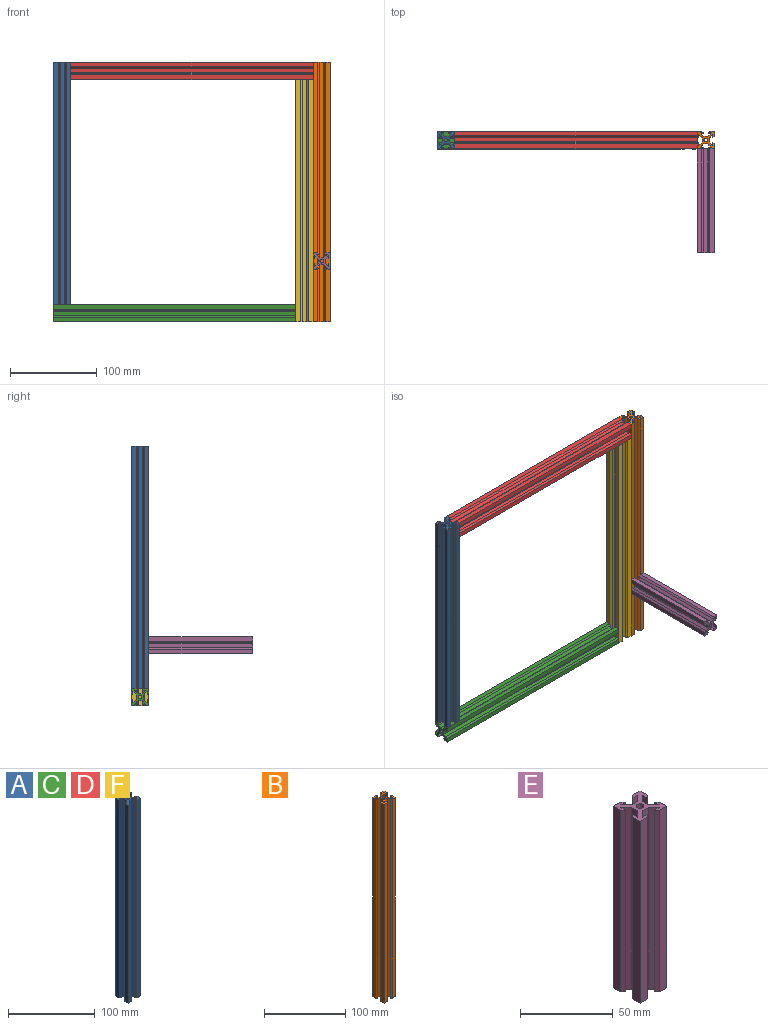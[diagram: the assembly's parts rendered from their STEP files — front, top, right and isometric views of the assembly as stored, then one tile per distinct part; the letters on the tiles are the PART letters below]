
ASSEMBLY  parts=6 mates=5
PART A: 39 faces, bbox 20x20x280 mm
  f0: plane 280x1.8mm, normal (-0.71,0.71,0), area 712.8mm2, adj f1,f35,f37,f38
  f1: plane 280x3.66mm, normal (0,-1,0), area 1023.5mm2, adj f0,f2,f37,f38
  f2: plane 280x4.2mm, normal (-0.71,0.71,0), area 1663.1mm2, adj f1,f3,f37,f38
  f3: plane 280x4.59mm, normal (0,1,0), area 1285.5mm2, adj f2,f4,f37,f38
  f4: plane 280x4.2mm, normal (0.71,0.71,0), area 1663.1mm2, adj f3,f5,f37,f38
  f5: plane 280x3.66mm, normal (0,-1,0), area 1023.5mm2, adj f4,f6,f37,f38
  f6: plane 280x1.8mm, normal (0.71,0.71,0), area 712.8mm2, adj f5,f7,f37,f38
  f7: plane 280x5.36mm, normal (0,1,0), area 1500.8mm2, adj f6,f8,f37,f38
  f8: plane 280x5.36mm, normal (-1,0,0), area 1500.8mm2, adj f7,f9,f37,f38
  f9: plane 280x1.8mm, normal (-0.71,-0.71,0), area 712.8mm2, adj f8,f10,f37,f38
  f10: plane 280x3.66mm, normal (1,0,0), area 1023.5mm2, adj f9,f11,f37,f38
  f11: plane 280x4.2mm, normal (-0.71,-0.71,0), area 1663.1mm2, adj f10,f12,f37,f38
  f12: plane 280x4.59mm, normal (-1,0,0), area 1285.5mm2, adj f11,f13,f37,f38
  f13: plane 280x4.2mm, normal (-0.71,0.71,0), area 1663.1mm2, adj f12,f14,f37,f38
  f14: plane 280x3.66mm, normal (1,0,0), area 1023.5mm2, adj f13,f15,f37,f38
  f15: plane 280x1.8mm, normal (-0.71,0.71,0), area 712.8mm2, adj f14,f16,f37,f38
  f16: plane 280x5.36mm, normal (-1,0,0), area 1500.8mm2, adj f15,f17,f37,f38
  f17: plane 280x5.36mm, normal (0,-1,0), area 1500.8mm2, adj f16,f18,f37,f38
  f18: plane 280x1.8mm, normal (0.71,-0.71,0), area 712.8mm2, adj f17,f19,f37,f38
  f19: plane 280x3.66mm, normal (0,1,0), area 1023.5mm2, adj f18,f20,f37,f38
  f20: plane 280x4.2mm, normal (0.71,-0.71,0), area 1663.1mm2, adj f19,f21,f37,f38
  f21: plane 280x4.59mm, normal (0,-1,0), area 1285.5mm2, adj f20,f22,f37,f38
  f22: plane 280x4.2mm, normal (-0.71,-0.71,0), area 1663.1mm2, adj f21,f23,f37,f38
  f23: plane 280x3.66mm, normal (0,1,0), area 1023.5mm2, adj f22,f24,f37,f38
  f24: plane 280x1.8mm, normal (-0.71,-0.71,0), area 712.8mm2, adj f23,f25,f37,f38
  f25: plane 280x5.36mm, normal (0,-1,0), area 1500.8mm2, adj f24,f26,f37,f38
  f26: plane 280x5.36mm, normal (1,0,0), area 1500.8mm2, adj f25,f27,f37,f38
  f27: plane 280x1.8mm, normal (0.71,0.71,0), area 712.8mm2, adj f26,f28,f37,f38
  f28: plane 280x3.66mm, normal (-1,0,0), area 1023.5mm2, adj f27,f29,f37,f38
  f29: plane 280x4.2mm, normal (0.71,0.71,0), area 1663.1mm2, adj f28,f30,f37,f38
  f30: plane 280x4.59mm, normal (1,0,0), area 1285.5mm2, adj f29,f31,f37,f38
  f31: plane 280x4.2mm, normal (0.71,-0.71,0), area 1663.1mm2, adj f30,f32,f37,f38
  f32: plane 280x3.66mm, normal (-1,0,0), area 1023.5mm2, adj f31,f33,f37,f38
  f33: plane 280x1.8mm, normal (0.71,-0.71,0), area 712.8mm2, adj f32,f34,f37,f38
  f34: plane 280x5.36mm, normal (1,0,0), area 1500.8mm2, adj f33,f35,f37,f38
  f35: plane 280x5.36mm, normal (0,1,0), area 1500.8mm2, adj f0,f34,f37,f38
  f36: cylinder r=2.1mm len=280mm, axis (0,0,-1), area 3694.5mm2, adj f37,f38
  f37: plane 20x20mm, normal (0,0,1), area 184.6mm2, adj f0,f1,f2,f3,f4,f5,f6,f7
  f38: plane 20x20mm, normal (0,0,-1), area 184.6mm2, adj f0,f1,f2,f3,f4,f5,f6,f7
PART B: 39 faces, bbox 20x20x300 mm
  f0: plane 300x1.8mm, normal (-0.71,-0.71,0), area 763.7mm2, adj f1,f35,f37,f38
  f1: plane 300x3.66mm, normal (1,0,0), area 1096.6mm2, adj f0,f2,f37,f38
  f2: plane 300x4.2mm, normal (-0.71,-0.71,0), area 1781.9mm2, adj f1,f3,f37,f38
  f3: plane 300x4.59mm, normal (-1,0,0), area 1377.3mm2, adj f2,f4,f37,f38
  f4: plane 300x4.2mm, normal (-0.71,0.71,0), area 1781.9mm2, adj f3,f5,f37,f38
  f5: plane 300x3.66mm, normal (1,0,0), area 1096.6mm2, adj f4,f6,f37,f38
  f6: plane 300x1.8mm, normal (-0.71,0.71,0), area 763.7mm2, adj f5,f7,f37,f38
  f7: plane 300x5.36mm, normal (-1,0,0), area 1608mm2, adj f6,f8,f37,f38
  f8: plane 300x5.36mm, normal (0,-1,0), area 1608mm2, adj f7,f9,f37,f38
  f9: plane 300x1.8mm, normal (0.71,-0.71,0), area 763.7mm2, adj f8,f10,f37,f38
  f10: plane 300x3.66mm, normal (0,1,0), area 1096.6mm2, adj f9,f11,f37,f38
  f11: plane 300x4.2mm, normal (0.71,-0.71,0), area 1781.9mm2, adj f10,f12,f37,f38
  f12: plane 300x4.59mm, normal (0,-1,0), area 1377.3mm2, adj f11,f13,f37,f38
  f13: plane 300x4.2mm, normal (-0.71,-0.71,0), area 1781.9mm2, adj f12,f14,f37,f38
  f14: plane 300x3.66mm, normal (0,1,0), area 1096.6mm2, adj f13,f15,f37,f38
  f15: plane 300x1.8mm, normal (-0.71,-0.71,0), area 763.7mm2, adj f14,f16,f37,f38
  f16: plane 300x5.36mm, normal (0,-1,0), area 1608mm2, adj f15,f17,f37,f38
  f17: plane 300x5.36mm, normal (1,0,0), area 1608mm2, adj f16,f18,f37,f38
  f18: plane 300x1.8mm, normal (0.71,0.71,0), area 763.7mm2, adj f17,f19,f37,f38
  f19: plane 300x3.66mm, normal (-1,0,0), area 1096.6mm2, adj f18,f20,f37,f38
  f20: plane 300x4.2mm, normal (0.71,0.71,0), area 1781.9mm2, adj f19,f21,f37,f38
  f21: plane 300x4.59mm, normal (1,0,0), area 1377.3mm2, adj f20,f22,f37,f38
  f22: plane 300x4.2mm, normal (0.71,-0.71,0), area 1781.9mm2, adj f21,f23,f37,f38
  f23: plane 300x3.66mm, normal (-1,0,0), area 1096.6mm2, adj f22,f24,f37,f38
  f24: plane 300x1.8mm, normal (0.71,-0.71,0), area 763.7mm2, adj f23,f25,f37,f38
  f25: plane 300x5.36mm, normal (1,0,0), area 1608mm2, adj f24,f26,f37,f38
  f26: plane 300x5.36mm, normal (0,1,0), area 1608mm2, adj f25,f27,f37,f38
  f27: plane 300x1.8mm, normal (-0.71,0.71,0), area 763.7mm2, adj f26,f28,f37,f38
  f28: plane 300x3.66mm, normal (0,-1,0), area 1096.6mm2, adj f27,f29,f37,f38
  f29: plane 300x4.2mm, normal (-0.71,0.71,0), area 1781.9mm2, adj f28,f30,f37,f38
  f30: plane 300x4.59mm, normal (0,1,0), area 1377.3mm2, adj f29,f31,f37,f38
  f31: plane 300x4.2mm, normal (0.71,0.71,0), area 1781.9mm2, adj f30,f32,f37,f38
  f32: plane 300x3.66mm, normal (0,-1,0), area 1096.6mm2, adj f31,f33,f37,f38
  f33: plane 300x1.8mm, normal (0.71,0.71,0), area 763.7mm2, adj f32,f34,f37,f38
  f34: plane 300x5.36mm, normal (0,1,0), area 1608mm2, adj f33,f35,f37,f38
  f35: plane 300x5.36mm, normal (-1,0,0), area 1608mm2, adj f0,f34,f37,f38
  f36: cylinder r=2.1mm len=300mm, axis (0,0,-1), area 3958.4mm2, adj f37,f38
  f37: plane 20x20mm, normal (0,0,1), area 184.6mm2, adj f0,f1,f2,f3,f4,f5,f6,f7
  f38: plane 20x20mm, normal (0,0,-1), area 184.6mm2, adj f0,f1,f2,f3,f4,f5,f6,f7
PART C: same geometry as A
PART D: same geometry as A
PART E: 39 faces, bbox 20x20x120 mm
  f0: plane 120x1.8mm, normal (-0.71,-0.71,0), area 305.5mm2, adj f1,f35,f37,f38
  f1: plane 120x3.66mm, normal (1,0,0), area 438.7mm2, adj f0,f2,f37,f38
  f2: plane 120x4.2mm, normal (-0.71,-0.71,0), area 712.8mm2, adj f1,f3,f37,f38
  f3: plane 120x4.59mm, normal (-1,0,0), area 550.9mm2, adj f2,f4,f37,f38
  f4: plane 120x4.2mm, normal (-0.71,0.71,0), area 712.8mm2, adj f3,f5,f37,f38
  f5: plane 120x3.66mm, normal (1,0,0), area 438.7mm2, adj f4,f6,f37,f38
  f6: plane 120x1.8mm, normal (-0.71,0.71,0), area 305.5mm2, adj f5,f7,f37,f38
  f7: plane 120x5.36mm, normal (-1,0,0), area 643.2mm2, adj f6,f8,f37,f38
  f8: plane 120x5.36mm, normal (0,-1,0), area 643.2mm2, adj f7,f9,f37,f38
  f9: plane 120x1.8mm, normal (0.71,-0.71,0), area 305.5mm2, adj f8,f10,f37,f38
  f10: plane 120x3.66mm, normal (0,1,0), area 438.7mm2, adj f9,f11,f37,f38
  f11: plane 120x4.2mm, normal (0.71,-0.71,0), area 712.8mm2, adj f10,f12,f37,f38
  f12: plane 120x4.59mm, normal (0,-1,0), area 550.9mm2, adj f11,f13,f37,f38
  f13: plane 120x4.2mm, normal (-0.71,-0.71,0), area 712.8mm2, adj f12,f14,f37,f38
  f14: plane 120x3.66mm, normal (0,1,0), area 438.7mm2, adj f13,f15,f37,f38
  f15: plane 120x1.8mm, normal (-0.71,-0.71,0), area 305.5mm2, adj f14,f16,f37,f38
  f16: plane 120x5.36mm, normal (0,-1,0), area 643.2mm2, adj f15,f17,f37,f38
  f17: plane 120x5.36mm, normal (1,0,0), area 643.2mm2, adj f16,f18,f37,f38
  f18: plane 120x1.8mm, normal (0.71,0.71,0), area 305.5mm2, adj f17,f19,f37,f38
  f19: plane 120x3.66mm, normal (-1,0,0), area 438.7mm2, adj f18,f20,f37,f38
  f20: plane 120x4.2mm, normal (0.71,0.71,0), area 712.8mm2, adj f19,f21,f37,f38
  f21: plane 120x4.59mm, normal (1,0,0), area 550.9mm2, adj f20,f22,f37,f38
  f22: plane 120x4.2mm, normal (0.71,-0.71,0), area 712.8mm2, adj f21,f23,f37,f38
  f23: plane 120x3.66mm, normal (-1,0,0), area 438.7mm2, adj f22,f24,f37,f38
  f24: plane 120x1.8mm, normal (0.71,-0.71,0), area 305.5mm2, adj f23,f25,f37,f38
  f25: plane 120x5.36mm, normal (1,0,0), area 643.2mm2, adj f24,f26,f37,f38
  f26: plane 120x5.36mm, normal (0,1,0), area 643.2mm2, adj f25,f27,f37,f38
  f27: plane 120x1.8mm, normal (-0.71,0.71,0), area 305.5mm2, adj f26,f28,f37,f38
  f28: plane 120x3.66mm, normal (0,-1,0), area 438.7mm2, adj f27,f29,f37,f38
  f29: plane 120x4.2mm, normal (-0.71,0.71,0), area 712.8mm2, adj f28,f30,f37,f38
  f30: plane 120x4.59mm, normal (0,1,0), area 550.9mm2, adj f29,f31,f37,f38
  f31: plane 120x4.2mm, normal (0.71,0.71,0), area 712.8mm2, adj f30,f32,f37,f38
  f32: plane 120x3.66mm, normal (0,-1,0), area 438.7mm2, adj f31,f33,f37,f38
  f33: plane 120x1.8mm, normal (0.71,0.71,0), area 305.5mm2, adj f32,f34,f37,f38
  f34: plane 120x5.36mm, normal (0,1,0), area 643.2mm2, adj f33,f35,f37,f38
  f35: plane 120x5.36mm, normal (-1,0,0), area 643.2mm2, adj f0,f34,f37,f38
  f36: cylinder r=2.1mm len=120mm, axis (0,0,-1), area 1583.4mm2, adj f37,f38
  f37: plane 20x20mm, normal (0,0,1), area 184.6mm2, adj f0,f1,f2,f3,f4,f5,f6,f7
  f38: plane 20x20mm, normal (0,0,-1), area 184.6mm2, adj f0,f1,f2,f3,f4,f5,f6,f7
PART F: same geometry as A
PLACE A t=(-219.2,66.84,-44.75)mm
PLACE B t=(230.8,66.84,-64.75)mm
PLACE C rot(axis=(0,-1,0),90deg) t=(275.8,66.84,-279.75)mm
PLACE D rot(axis=(-0.58,-0.58,0.58),120deg) t=(295.8,-158.16,225.25)mm
PLACE E rot(axis=(1,0,0),90deg) t=(305.8,56.84,5.25)mm
PLACE F t=(60.8,66.84,-64.75)mm
MATE fastened B.f35 <-> D.f38  axis (-1,0,0) through (295.8,76.84,235.25)mm
MATE fastened E.f38 <-> B.f8  axis (0,1,0) through (295.8,56.84,-4.75)mm
MATE fastened F.f37 <-> D.f35  axis (0,0,1) through (295.8,76.84,215.25)mm
MATE fastened C.f38 <-> F.f16  axis (1,0,0) through (275.8,56.84,-64.75)mm
MATE fastened D.f37 <-> A.f26  axis (-1,0,0) through (15.8,56.84,235.25)mm
